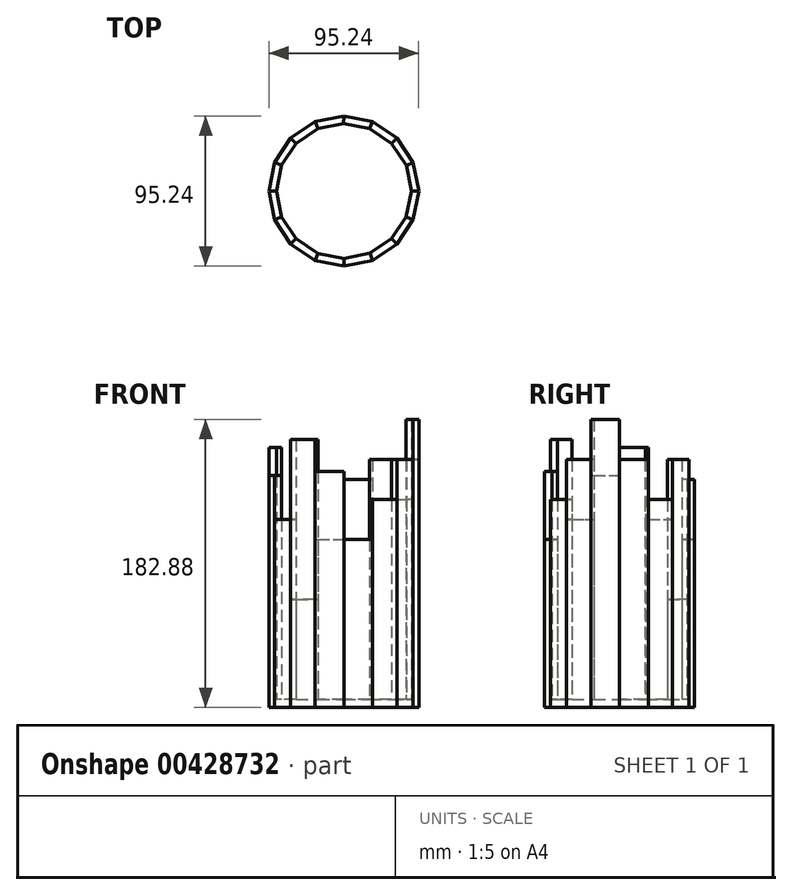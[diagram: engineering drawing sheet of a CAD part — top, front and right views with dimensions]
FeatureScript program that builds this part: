
annotation { "Feature Type Name" : "Feature", "Feature Type Description" : "" }
export const myFeature = defineFeature(function(context is Context, id is Id, definition is map)
    precondition{}
    {
        {
            var Q0;
            Q0=qCreatedBy(makeId("Top.planeOp"),FACE);
            var sketch = newSketch(context, id + "F0", { "sketchPlane" : qUnion([Q0])});
            skLineSegment(sketch, "E0", {"start": v(0, 0) * mm, "end": v(0, 47.63) * mm});
            skLineSegment(sketch, "E1", {"start": v(0, 47.63) * mm, "end": v(0, 0) * mm});
            skLineSegment(sketch, "E2", {"start": v(0, -47.63) * mm, "end": v(0, 0) * mm});
            skLineSegment(sketch, "E3", {"start": v(-47.63, 0) * mm, "end": v(47.63, 0) * mm});
            skLineSegment(sketch, "E4", {"start": v(0, 0) * mm, "end": v(-33.68, 33.68) * mm});
            skLineSegment(sketch, "E5", {"start": v(-33.68, 33.68) * mm, "end": v(0, 0) * mm});
            skLineSegment(sketch, "E6", {"start": v(0, 0) * mm, "end": v(33.68, -33.68) * mm});
            skLineSegment(sketch, "E7", {"start": v(0, 0) * mm, "end": v(33.68, 33.68) * mm});
            skLineSegment(sketch, "E8", {"start": v(0, 0) * mm, "end": v(18.23, 44) * mm});
            skLineSegment(sketch, "E9", {"start": v(0, 0) * mm, "end": v(44, 18.23) * mm});
            skLineSegment(sketch, "E10", {"start": v(0, 0) * mm, "end": v(44, -18.23) * mm});
            skLineSegment(sketch, "E11", {"start": v(0, 0) * mm, "end": v(18.23, -44) * mm});
            skLineSegment(sketch, "E12", {"start": v(0, 0) * mm, "end": v(-33.68, -33.68) * mm});
            skLineSegment(sketch, "E13", {"start": v(0, 0) * mm, "end": v(-18.23, -44) * mm});
            skLineSegment(sketch, "E14", {"start": v(0, 0) * mm, "end": v(-44, -18.23) * mm});
            skLineSegment(sketch, "E15", {"start": v(0, 0) * mm, "end": v(-44, 18.23) * mm});
            skLineSegment(sketch, "E16", {"start": v(0, 0) * mm, "end": v(-18.23, 44) * mm});
            skLineSegment(sketch, "E17", {"start": v(-47.63, 0) * mm, "end": v(-44, 18.23) * mm});
            skLineSegment(sketch, "E18", {"start": v(-44, 18.23) * mm, "end": v(-33.68, 33.68) * mm});
            skLineSegment(sketch, "E19", {"start": v(-18.23, 44) * mm, "end": v(-33.68, 33.68) * mm});
            skLineSegment(sketch, "E20", {"start": v(-18.23, 44) * mm, "end": v(0, 47.63) * mm});
            skLineSegment(sketch, "E21", {"start": v(0, 47.63) * mm, "end": v(18.23, 44) * mm});
            skLineSegment(sketch, "E22", {"start": v(18.23, 44) * mm, "end": v(33.68, 33.68) * mm});
            skLineSegment(sketch, "E23", {"start": v(33.68, 33.68) * mm, "end": v(44, 18.23) * mm});
            skLineSegment(sketch, "E24", {"start": v(44, 18.23) * mm, "end": v(47.63, 0) * mm});
            skLineSegment(sketch, "E25", {"start": v(47.63, 0) * mm, "end": v(44, -18.23) * mm});
            skLineSegment(sketch, "E26", {"start": v(44, -18.23) * mm, "end": v(33.68, -33.68) * mm});
            skLineSegment(sketch, "E27", {"start": v(33.68, -33.68) * mm, "end": v(18.23, -44) * mm});
            skLineSegment(sketch, "E28", {"start": v(18.23, -44) * mm, "end": v(0, -47.63) * mm});
            skLineSegment(sketch, "E29", {"start": v(0, -47.63) * mm, "end": v(-18.23, -44) * mm});
            skLineSegment(sketch, "E30", {"start": v(-18.23, -44) * mm, "end": v(-33.68, -33.68) * mm});
            skLineSegment(sketch, "E31", {"start": v(-33.68, -33.68) * mm, "end": v(-44, -18.23) * mm});
            skLineSegment(sketch, "E32", {"start": v(-44, -18.23) * mm, "end": v(-47.63, 0) * mm});
            skLineSegment(sketch, "E33", {"start": v(-39.6, 16.4) * mm, "end": v(-30.3, 30.3) * mm});
            skLineSegment(sketch, "E34", {"start": v(-30.3, 30.3) * mm, "end": v(-16.4, 39.6) * mm});
            skLineSegment(sketch, "E35", {"start": v(-16.4, 39.6) * mm, "end": v(-0.14, 42.86) * mm});
            skLineSegment(sketch, "E36", {"start": v(-0.14, 42.86) * mm, "end": v(16.4, 39.6) * mm});
            skLineSegment(sketch, "E37", {"start": v(16.4, 39.6) * mm, "end": v(30.3, 30.3) * mm});
            skLineSegment(sketch, "E38", {"start": v(30.3, 30.3) * mm, "end": v(39.69, 16.2) * mm});
            skLineSegment(sketch, "E39", {"start": v(39.69, 16.2) * mm, "end": v(42.86, 0) * mm});
            skLineSegment(sketch, "E40", {"start": v(42.86, 0) * mm, "end": v(39.6, -16.4) * mm});
            skLineSegment(sketch, "E41", {"start": v(39.6, -16.4) * mm, "end": v(30.3, -30.3) * mm});
            skLineSegment(sketch, "E42", {"start": v(30.3, -30.3) * mm, "end": v(16.68, -39.48) * mm});
            skLineSegment(sketch, "E43", {"start": v(16.68, -39.48) * mm, "end": v(0, -42.86) * mm});
            skLineSegment(sketch, "E44", {"start": v(0, -42.86) * mm, "end": v(-16.4, -39.6) * mm});
            skLineSegment(sketch, "E45", {"start": v(-16.4, -39.6) * mm, "end": v(-30.3, -30.3) * mm});
            skLineSegment(sketch, "E46", {"start": v(-30.3, -30.3) * mm, "end": v(-39.6, -16.4) * mm});
            skLineSegment(sketch, "E47", {"start": v(-39.6, -16.4) * mm, "end": v(-42.86, 0) * mm});
            skLineSegment(sketch, "E48", {"start": v(-42.86, 0) * mm, "end": v(-39.6, 16.4) * mm});
            skSolve(sketch);
        }
        {
            var Q0;
            {var subQ1=sQuery(id+"F0.wireOp",EDGE,"E20");Q0=makeQuery(id+"F0.imprint","IMPRINT",FACE,{"disambiguationData":[TD([[makeQuery(id+"F0.imprint","IMPRINT",EDGE,{"derivedFrom":subQ1}),-1.0]])]});}
            var Q1;
            {var subQ0=sQuery(id+"F0.wireOp",EDGE,"E28");Q1=makeQuery(id+"F0.imprint","IMPRINT",FACE,{"disambiguationData":[TD([[makeQuery(id+"F0.imprint","IMPRINT",EDGE,{"derivedFrom":subQ0}),-1.0]])]});}
            var Q2;
            {var subQ0=sQuery(id+"F0.wireOp",EDGE,"E32");Q2=makeQuery(id+"F0.imprint","IMPRINT",FACE,{"disambiguationData":[TD([[makeQuery(id+"F0.imprint","IMPRINT",EDGE,{"derivedFrom":subQ0}),-1.0]])]});}
            var Q3;
            {var subQ4=sQuery(id+"F0.wireOp",EDGE,"E24");Q3=makeQuery(id+"F0.imprint","IMPRINT",FACE,{"disambiguationData":[TD([[makeQuery(id+"F0.imprint","IMPRINT",EDGE,{"derivedFrom":subQ4}),-1.0]])]});}
            var Q4;
            {var subQ0=sQuery(id+"F0.wireOp",EDGE,"E26");Q4=makeQuery(id+"F0.imprint","IMPRINT",FACE,{"disambiguationData":[TD([[makeQuery(id+"F0.imprint","IMPRINT",EDGE,{"derivedFrom":subQ0}),-1.0]])]});}
            var Q5;
            {var subQ0=sQuery(id+"F0.wireOp",EDGE,"E18");Q5=makeQuery(id+"F0.imprint","IMPRINT",FACE,{"disambiguationData":[TD([[makeQuery(id+"F0.imprint","IMPRINT",EDGE,{"derivedFrom":subQ0}),-1.0]])]});}
            var Q6;
            {var subQ0=sQuery(id+"F0.wireOp",EDGE,"E30");Q6=makeQuery(id+"F0.imprint","IMPRINT",FACE,{"disambiguationData":[TD([[makeQuery(id+"F0.imprint","IMPRINT",EDGE,{"derivedFrom":subQ0}),-1.0]])]});}
            var Q7;
            {var subQ0=sQuery(id+"F0.wireOp",EDGE,"E22");Q7=makeQuery(id+"F0.imprint","IMPRINT",FACE,{"disambiguationData":[TD([[makeQuery(id+"F0.imprint","IMPRINT",EDGE,{"derivedFrom":subQ0}),-1.0]])]});}
            var Q8;
            {var subQ0=sQuery(id+"F0.wireOp",EDGE,"E29");Q8=makeQuery(id+"F0.imprint","IMPRINT",FACE,{"disambiguationData":[TD([[makeQuery(id+"F0.imprint","IMPRINT",EDGE,{"derivedFrom":subQ0}),-1.0]])]});}
            var Q9;
            {var subQ0=sQuery(id+"F0.wireOp",EDGE,"E21");Q9=makeQuery(id+"F0.imprint","IMPRINT",FACE,{"disambiguationData":[TD([[makeQuery(id+"F0.imprint","IMPRINT",EDGE,{"derivedFrom":subQ0}),-1.0]])]});}
            var Q10;
            {var subQ0=sQuery(id+"F0.wireOp",EDGE,"E31");Q10=makeQuery(id+"F0.imprint","IMPRINT",FACE,{"disambiguationData":[TD([[makeQuery(id+"F0.imprint","IMPRINT",EDGE,{"derivedFrom":subQ0}),-1.0]])]});}
            var Q11;
            {var subQ0=sQuery(id+"F0.wireOp",EDGE,"E23");Q11=makeQuery(id+"F0.imprint","IMPRINT",FACE,{"disambiguationData":[TD([[makeQuery(id+"F0.imprint","IMPRINT",EDGE,{"derivedFrom":subQ0}),-1.0]])]});}
            var Q12;
            {var subQ1=sQuery(id+"F0.wireOp",EDGE,"E27");Q12=makeQuery(id+"F0.imprint","IMPRINT",FACE,{"disambiguationData":[TD([[makeQuery(id+"F0.imprint","IMPRINT",EDGE,{"derivedFrom":subQ1}),-1.0]])]});}
            var Q13;
            {var subQ0=sQuery(id+"F0.wireOp",EDGE,"E19");Q13=makeQuery(id+"F0.imprint","IMPRINT",FACE,{"disambiguationData":[TD([[makeQuery(id+"F0.imprint","IMPRINT",EDGE,{"derivedFrom":subQ0}),1.0]])]});}
            var Q14;
            {var subQ0=sQuery(id+"F0.wireOp",EDGE,"E17");Q14=makeQuery(id+"F0.imprint","IMPRINT",FACE,{"disambiguationData":[TD([[makeQuery(id+"F0.imprint","IMPRINT",EDGE,{"derivedFrom":subQ0}),-1.0]])]});}
            var Q15;
            {var subQ0=sQuery(id+"F0.wireOp",EDGE,"E25");Q15=makeQuery(id+"F0.imprint","IMPRINT",FACE,{"disambiguationData":[TD([[makeQuery(id+"F0.imprint","IMPRINT",EDGE,{"derivedFrom":subQ0}),-1.0]])]});}
            extrude(context, id + "F1", {"entities" : qUnion([Q0, Q1, Q2, Q3, Q4, Q5, Q6, Q7, Q8, Q9, Q10, Q11, Q12, Q13, Q14, Q15]), "depth" : 152.4 * mm});
        }
        {
            var Q0;
            Q0=makeQuery(id+"F1.opExtrude","CAP_FACE",FACE,{"disambiguationData":[OSD([sQuery(id+"F0.wireOp",EDGE,"E17"),sQuery(id+"F0.wireOp",EDGE,"E18"),sQuery(id+"F0.wireOp",EDGE,"E19"),sQuery(id+"F0.wireOp",EDGE,"E20"),sQuery(id+"F0.wireOp",EDGE,"E21"),sQuery(id+"F0.wireOp",EDGE,"E22"),sQuery(id+"F0.wireOp",EDGE,"E23"),sQuery(id+"F0.wireOp",EDGE,"E24"),sQuery(id+"F0.wireOp",EDGE,"E25"),sQuery(id+"F0.wireOp",EDGE,"E26"),sQuery(id+"F0.wireOp",EDGE,"E27"),sQuery(id+"F0.wireOp",EDGE,"E28"),sQuery(id+"F0.wireOp",EDGE,"E29"),sQuery(id+"F0.wireOp",EDGE,"E30"),sQuery(id+"F0.wireOp",EDGE,"E31"),sQuery(id+"F0.wireOp",EDGE,"E32"),sQuery(id+"F0.wireOp",EDGE,"E33"),sQuery(id+"F0.wireOp",EDGE,"E34"),sQuery(id+"F0.wireOp",EDGE,"E35"),sQuery(id+"F0.wireOp",EDGE,"E36"),sQuery(id+"F0.wireOp",EDGE,"E37"),sQuery(id+"F0.wireOp",EDGE,"E38"),sQuery(id+"F0.wireOp",EDGE,"E39"),sQuery(id+"F0.wireOp",EDGE,"E40"),sQuery(id+"F0.wireOp",EDGE,"E41"),sQuery(id+"F0.wireOp",EDGE,"E42"),sQuery(id+"F0.wireOp",EDGE,"E43"),sQuery(id+"F0.wireOp",EDGE,"E44"),sQuery(id+"F0.wireOp",EDGE,"E45"),sQuery(id+"F0.wireOp",EDGE,"E46"),sQuery(id+"F0.wireOp",EDGE,"E47"),sQuery(id+"F0.wireOp",EDGE,"E48")])],"isStart":false});
            var sketch = newSketch(context, id + "F2", { "sketchPlane" : qUnion([Q0])});
            skLineSegment(sketch, "E49", {"start": v(-18.23, -44) * mm, "end": v(-16.4, -39.6) * mm});
            skLineSegment(sketch, "E50", {"start": v(0, -47.63) * mm, "end": v(0, -42.86) * mm});
            skLineSegment(sketch, "E51", {"start": v(18.23, -44) * mm, "end": v(16.68, -39.48) * mm});
            skLineSegment(sketch, "E52", {"start": v(33.68, -33.68) * mm, "end": v(30.3, -30.3) * mm});
            skLineSegment(sketch, "E53", {"start": v(44, -18.23) * mm, "end": v(39.6, -16.4) * mm});
            skLineSegment(sketch, "E54", {"start": v(47.63, 0) * mm, "end": v(42.86, 0) * mm});
            skLineSegment(sketch, "E55", {"start": v(44, 18.23) * mm, "end": v(39.69, 16.2) * mm});
            skLineSegment(sketch, "E56", {"start": v(33.68, 33.68) * mm, "end": v(30.3, 30.3) * mm});
            skLineSegment(sketch, "E57", {"start": v(18.23, 44) * mm, "end": v(16.4, 39.6) * mm});
            skLineSegment(sketch, "E58", {"start": v(0, 47.63) * mm, "end": v(-0.14, 42.86) * mm});
            skLineSegment(sketch, "E59", {"start": v(-18.23, 44) * mm, "end": v(-16.4, 39.6) * mm});
            skLineSegment(sketch, "E60", {"start": v(-33.68, 33.68) * mm, "end": v(-30.3, 30.3) * mm});
            skLineSegment(sketch, "E61", {"start": v(-39.6, 16.4) * mm, "end": v(-44, 18.23) * mm});
            skLineSegment(sketch, "E62", {"start": v(-47.63, 0) * mm, "end": v(-42.86, 0) * mm});
            skLineSegment(sketch, "E63", {"start": v(-39.6, -16.4) * mm, "end": v(-44, -18.23) * mm});
            skLineSegment(sketch, "E64", {"start": v(-30.3, -30.3) * mm, "end": v(-33.68, -33.68) * mm});
            skSolve(sketch);
        }
        {
            var Q0;
            Q0=makeQuery(id+"F2.imprint","IMPRINT",FACE,{"disambiguationData":[TD([[makeQuery(id+"F2.imprint","IMPRINT",EDGE,{"derivedFrom":sQuery(id+"F2.wireOp",EDGE,"E55")}),-1.0]])]});
            extrude(context, id + "F3", {"entities" : qUnion([Q0]), "operationType" : NewBodyOperationType.REMOVE, "oppositeDirection" : true, "depth" : 25.4 * mm});
        }
        {
            var Q0;
            Q0=makeQuery(id+"F1.opExtrude","CAP_FACE",FACE,{"disambiguationData":[OSD([sQuery(id+"F0.wireOp",EDGE,"E17"),sQuery(id+"F0.wireOp",EDGE,"E18"),sQuery(id+"F0.wireOp",EDGE,"E19"),sQuery(id+"F0.wireOp",EDGE,"E20"),sQuery(id+"F0.wireOp",EDGE,"E21"),sQuery(id+"F0.wireOp",EDGE,"E22"),sQuery(id+"F0.wireOp",EDGE,"E23"),sQuery(id+"F0.wireOp",EDGE,"E24"),sQuery(id+"F0.wireOp",EDGE,"E25"),sQuery(id+"F0.wireOp",EDGE,"E26"),sQuery(id+"F0.wireOp",EDGE,"E27"),sQuery(id+"F0.wireOp",EDGE,"E28"),sQuery(id+"F0.wireOp",EDGE,"E29"),sQuery(id+"F0.wireOp",EDGE,"E30"),sQuery(id+"F0.wireOp",EDGE,"E31"),sQuery(id+"F0.wireOp",EDGE,"E32"),sQuery(id+"F0.wireOp",EDGE,"E33"),sQuery(id+"F0.wireOp",EDGE,"E34"),sQuery(id+"F0.wireOp",EDGE,"E35"),sQuery(id+"F0.wireOp",EDGE,"E36"),sQuery(id+"F0.wireOp",EDGE,"E37"),sQuery(id+"F0.wireOp",EDGE,"E38"),sQuery(id+"F0.wireOp",EDGE,"E39"),sQuery(id+"F0.wireOp",EDGE,"E40"),sQuery(id+"F0.wireOp",EDGE,"E41"),sQuery(id+"F0.wireOp",EDGE,"E42"),sQuery(id+"F0.wireOp",EDGE,"E43"),sQuery(id+"F0.wireOp",EDGE,"E44"),sQuery(id+"F0.wireOp",EDGE,"E45"),sQuery(id+"F0.wireOp",EDGE,"E46"),sQuery(id+"F0.wireOp",EDGE,"E47"),sQuery(id+"F0.wireOp",EDGE,"E48")])],"isStart":false});
            var sketch = newSketch(context, id + "F4", { "sketchPlane" : qUnion([Q0])});
            skLineSegment(sketch, "E65", {"start": v(0, 47.63) * mm, "end": v(-0.14, 42.86) * mm});
            skLineSegment(sketch, "E66", {"start": v(-18.23, 44) * mm, "end": v(-16.4, 39.6) * mm});
            skSolve(sketch);
        }
        {
            var Q0;
            Q0=makeQuery(id+"F4.imprint","IMPRINT",FACE,{"disambiguationData":[TD([[makeQuery(id+"F4.imprint","IMPRINT",EDGE,{"derivedFrom":sQuery(id+"F4.wireOp",EDGE,"E65")}),-1.0]])]});
            extrude(context, id + "F5", {"entities" : qUnion([Q0]), "operationType" : NewBodyOperationType.REMOVE, "oppositeDirection" : true, "depth" : 50.8 * mm});
        }
        {
            var Q0;
            {var subQ0=sQuery(id+"F0.wireOp",EDGE,"E37");var subQ1=sQuery(id+"F0.wireOp",EDGE,"E22");var subQ2=sQuery(id+"F0.wireOp",EDGE,"E36");var subQ3=sQuery(id+"F0.wireOp",EDGE,"E21");Q0=makeQuery(id+"F5.boolean.opBoolean","SPLIT",FACE,{"disambiguationData":[TD([makeQuery(id+"F1.opExtrude","SWEPT_FACE",FACE,{"disambiguationData":[OSD([subQ3])]})])],"derivedFrom":makeQuery(id+"F1.opExtrude","CAP_FACE",FACE,{"disambiguationData":[OSD([sQuery(id+"F0.wireOp",EDGE,"E17"),sQuery(id+"F0.wireOp",EDGE,"E18"),sQuery(id+"F0.wireOp",EDGE,"E19"),sQuery(id+"F0.wireOp",EDGE,"E20"),subQ3,subQ1,sQuery(id+"F0.wireOp",EDGE,"E23"),sQuery(id+"F0.wireOp",EDGE,"E24"),sQuery(id+"F0.wireOp",EDGE,"E25"),sQuery(id+"F0.wireOp",EDGE,"E26"),sQuery(id+"F0.wireOp",EDGE,"E27"),sQuery(id+"F0.wireOp",EDGE,"E28"),sQuery(id+"F0.wireOp",EDGE,"E29"),sQuery(id+"F0.wireOp",EDGE,"E30"),sQuery(id+"F0.wireOp",EDGE,"E31"),sQuery(id+"F0.wireOp",EDGE,"E32"),sQuery(id+"F0.wireOp",EDGE,"E33"),sQuery(id+"F0.wireOp",EDGE,"E34"),sQuery(id+"F0.wireOp",EDGE,"E35"),subQ2,subQ0,sQuery(id+"F0.wireOp",EDGE,"E38"),sQuery(id+"F0.wireOp",EDGE,"E39"),sQuery(id+"F0.wireOp",EDGE,"E40"),sQuery(id+"F0.wireOp",EDGE,"E41"),sQuery(id+"F0.wireOp",EDGE,"E42"),sQuery(id+"F0.wireOp",EDGE,"E43"),sQuery(id+"F0.wireOp",EDGE,"E44"),sQuery(id+"F0.wireOp",EDGE,"E45"),sQuery(id+"F0.wireOp",EDGE,"E46"),sQuery(id+"F0.wireOp",EDGE,"E47"),sQuery(id+"F0.wireOp",EDGE,"E48")])],"isStart":false})});}
            var sketch = newSketch(context, id + "F6", { "sketchPlane" : qUnion([Q0])});
            skLineSegment(sketch, "E67", {"start": v(18.23, 44) * mm, "end": v(16.4, 39.6) * mm});
            skSolve(sketch);
        }
        {
            var Q0;
            Q0=makeQuery(id+"F6.imprint","IMPRINT",FACE,{"disambiguationData":[TD([[makeQuery(id+"F6.imprint","IMPRINT",EDGE,{"derivedFrom":sQuery(id+"F6.wireOp",EDGE,"E67")}),-1.0]])]});
            extrude(context, id + "F7", {"entities" : qUnion([Q0]), "operationType" : NewBodyOperationType.REMOVE, "oppositeDirection" : true, "depth" : 12.7 * mm});
        }
        {
            var Q0;
            {var subQ0=sQuery(id+"F0.wireOp",EDGE,"E46");var subQ1=sQuery(id+"F0.wireOp",EDGE,"E45");var subQ2=sQuery(id+"F0.wireOp",EDGE,"E44");var subQ3=sQuery(id+"F0.wireOp",EDGE,"E43");var subQ4=sQuery(id+"F0.wireOp",EDGE,"E40");var subQ5=sQuery(id+"F0.wireOp",EDGE,"E39");var subQ6=sQuery(id+"F0.wireOp",EDGE,"E34");var subQ7=sQuery(id+"F0.wireOp",EDGE,"E33");var subQ8=sQuery(id+"F0.wireOp",EDGE,"E32");var subQ9=sQuery(id+"F0.wireOp",EDGE,"E31");var subQ10=sQuery(id+"F0.wireOp",EDGE,"E24");var subQ11=sQuery(id+"F0.wireOp",EDGE,"E42");var subQ12=sQuery(id+"F0.wireOp",EDGE,"E19");var subQ13=sQuery(id+"F0.wireOp",EDGE,"E30");var subQ14=sQuery(id+"F0.wireOp",EDGE,"E41");var subQ15=sQuery(id+"F0.wireOp",EDGE,"E18");var subQ16=sQuery(id+"F0.wireOp",EDGE,"E29");var subQ17=sQuery(id+"F0.wireOp",EDGE,"E17");var subQ18=sQuery(id+"F0.wireOp",EDGE,"E26");var subQ19=sQuery(id+"F0.wireOp",EDGE,"E25");var subQ20=sQuery(id+"F0.wireOp",EDGE,"E27");var subQ21=sQuery(id+"F0.wireOp",EDGE,"E28");var subQ22=sQuery(id+"F0.wireOp",EDGE,"E47");var subQ23=sQuery(id+"F0.wireOp",EDGE,"E48");Q0=makeQuery(id+"F5.boolean.opBoolean","SPLIT",FACE,{"disambiguationData":[TD([makeQuery(id+"F1.opExtrude","SWEPT_FACE",FACE,{"disambiguationData":[OSD([subQ17])]})])],"derivedFrom":makeQuery(id+"F1.opExtrude","CAP_FACE",FACE,{"disambiguationData":[OSD([subQ17,subQ15,subQ12,sQuery(id+"F0.wireOp",EDGE,"E20"),sQuery(id+"F0.wireOp",EDGE,"E21"),sQuery(id+"F0.wireOp",EDGE,"E22"),sQuery(id+"F0.wireOp",EDGE,"E23"),subQ10,subQ19,subQ18,subQ20,subQ21,subQ16,subQ13,subQ9,subQ8,subQ7,subQ6,sQuery(id+"F0.wireOp",EDGE,"E35"),sQuery(id+"F0.wireOp",EDGE,"E36"),sQuery(id+"F0.wireOp",EDGE,"E37"),sQuery(id+"F0.wireOp",EDGE,"E38"),subQ5,subQ4,subQ14,subQ11,subQ3,subQ2,subQ1,subQ0,subQ22,subQ23])],"isStart":false})});}
            var sketch = newSketch(context, id + "F8", { "sketchPlane" : qUnion([Q0])});
            skLineSegment(sketch, "E68", {"start": v(-33.68, 33.68) * mm, "end": v(-30.3, 30.3) * mm});
            skSolve(sketch);
        }
        {
            var Q0;
            Q0=makeQuery(id+"F8.imprint","IMPRINT",FACE,{"disambiguationData":[TD([[makeQuery(id+"F8.imprint","IMPRINT",EDGE,{"derivedFrom":sQuery(id+"F8.wireOp",EDGE,"E68")}),1.0]])]});
            extrude(context, id + "F9", {"entities" : qUnion([Q0]), "operationType" : NewBodyOperationType.REMOVE, "oppositeDirection" : true, "depth" : 63.5 * mm});
        }
        {
            var Q0;
            {var subQ0=sQuery(id+"F0.wireOp",EDGE,"E46");var subQ1=sQuery(id+"F0.wireOp",EDGE,"E45");var subQ2=sQuery(id+"F0.wireOp",EDGE,"E44");var subQ3=sQuery(id+"F0.wireOp",EDGE,"E43");var subQ4=sQuery(id+"F0.wireOp",EDGE,"E40");var subQ5=sQuery(id+"F0.wireOp",EDGE,"E39");var subQ6=sQuery(id+"F0.wireOp",EDGE,"E34");var subQ7=sQuery(id+"F0.wireOp",EDGE,"E33");var subQ8=sQuery(id+"F0.wireOp",EDGE,"E32");var subQ9=sQuery(id+"F0.wireOp",EDGE,"E31");var subQ10=sQuery(id+"F0.wireOp",EDGE,"E24");var subQ11=sQuery(id+"F0.wireOp",EDGE,"E42");var subQ12=sQuery(id+"F0.wireOp",EDGE,"E19");var subQ13=sQuery(id+"F0.wireOp",EDGE,"E30");var subQ14=sQuery(id+"F0.wireOp",EDGE,"E41");var subQ15=sQuery(id+"F0.wireOp",EDGE,"E18");var subQ16=sQuery(id+"F0.wireOp",EDGE,"E29");var subQ17=sQuery(id+"F0.wireOp",EDGE,"E17");var subQ18=sQuery(id+"F0.wireOp",EDGE,"E26");var subQ19=sQuery(id+"F0.wireOp",EDGE,"E25");var subQ20=sQuery(id+"F0.wireOp",EDGE,"E27");var subQ21=sQuery(id+"F0.wireOp",EDGE,"E28");var subQ22=sQuery(id+"F0.wireOp",EDGE,"E47");var subQ23=sQuery(id+"F0.wireOp",EDGE,"E48");Q0=makeQuery(id+"F5.boolean.opBoolean","SPLIT",FACE,{"disambiguationData":[TD([makeQuery(id+"F1.opExtrude","SWEPT_FACE",FACE,{"disambiguationData":[OSD([subQ17])]})])],"derivedFrom":makeQuery(id+"F1.opExtrude","CAP_FACE",FACE,{"disambiguationData":[OSD([subQ17,subQ15,subQ12,sQuery(id+"F0.wireOp",EDGE,"E20"),sQuery(id+"F0.wireOp",EDGE,"E21"),sQuery(id+"F0.wireOp",EDGE,"E22"),sQuery(id+"F0.wireOp",EDGE,"E23"),subQ10,subQ19,subQ18,subQ20,subQ21,subQ16,subQ13,subQ9,subQ8,subQ7,subQ6,sQuery(id+"F0.wireOp",EDGE,"E35"),sQuery(id+"F0.wireOp",EDGE,"E36"),sQuery(id+"F0.wireOp",EDGE,"E37"),sQuery(id+"F0.wireOp",EDGE,"E38"),subQ5,subQ4,subQ14,subQ11,subQ3,subQ2,subQ1,subQ0,subQ22,subQ23])],"isStart":false})});}
            var sketch = newSketch(context, id + "F10", { "sketchPlane" : qUnion([Q0])});
            skLineSegment(sketch, "E69", {"start": v(-44, 18.23) * mm, "end": v(-39.6, 16.4) * mm});
            skSolve(sketch);
        }
        {
            var Q0;
            Q0=makeQuery(id+"F10.imprint","IMPRINT",FACE,{"disambiguationData":[TD([[makeQuery(id+"F10.imprint","IMPRINT",EDGE,{"derivedFrom":sQuery(id+"F10.wireOp",EDGE,"E69")}),1.0]])]});
            extrude(context, id + "F11", {"entities" : qUnion([Q0]), "operationType" : NewBodyOperationType.REMOVE, "oppositeDirection" : true, "depth" : 38.1 * mm});
        }
        {
            var Q0;
            {var subQ0=sQuery(id+"F0.wireOp",EDGE,"E46");var subQ1=sQuery(id+"F0.wireOp",EDGE,"E45");var subQ2=sQuery(id+"F0.wireOp",EDGE,"E44");var subQ3=sQuery(id+"F0.wireOp",EDGE,"E43");var subQ4=sQuery(id+"F0.wireOp",EDGE,"E40");var subQ5=sQuery(id+"F0.wireOp",EDGE,"E39");var subQ6=sQuery(id+"F0.wireOp",EDGE,"E34");var subQ7=sQuery(id+"F0.wireOp",EDGE,"E33");var subQ8=sQuery(id+"F0.wireOp",EDGE,"E32");var subQ9=sQuery(id+"F0.wireOp",EDGE,"E31");var subQ10=sQuery(id+"F0.wireOp",EDGE,"E24");var subQ11=sQuery(id+"F0.wireOp",EDGE,"E42");var subQ12=sQuery(id+"F0.wireOp",EDGE,"E19");var subQ13=sQuery(id+"F0.wireOp",EDGE,"E30");var subQ14=sQuery(id+"F0.wireOp",EDGE,"E41");var subQ15=sQuery(id+"F0.wireOp",EDGE,"E18");var subQ16=sQuery(id+"F0.wireOp",EDGE,"E29");var subQ17=sQuery(id+"F0.wireOp",EDGE,"E17");var subQ18=sQuery(id+"F0.wireOp",EDGE,"E26");var subQ19=sQuery(id+"F0.wireOp",EDGE,"E25");var subQ20=sQuery(id+"F0.wireOp",EDGE,"E27");var subQ21=sQuery(id+"F0.wireOp",EDGE,"E28");var subQ22=sQuery(id+"F0.wireOp",EDGE,"E47");var subQ23=sQuery(id+"F0.wireOp",EDGE,"E48");Q0=makeQuery(id+"F5.boolean.opBoolean","SPLIT",FACE,{"disambiguationData":[TD([makeQuery(id+"F1.opExtrude","SWEPT_FACE",FACE,{"disambiguationData":[OSD([subQ17])]})])],"derivedFrom":makeQuery(id+"F1.opExtrude","CAP_FACE",FACE,{"disambiguationData":[OSD([subQ17,subQ15,subQ12,sQuery(id+"F0.wireOp",EDGE,"E20"),sQuery(id+"F0.wireOp",EDGE,"E21"),sQuery(id+"F0.wireOp",EDGE,"E22"),sQuery(id+"F0.wireOp",EDGE,"E23"),subQ10,subQ19,subQ18,subQ20,subQ21,subQ16,subQ13,subQ9,subQ8,subQ7,subQ6,sQuery(id+"F0.wireOp",EDGE,"E35"),sQuery(id+"F0.wireOp",EDGE,"E36"),sQuery(id+"F0.wireOp",EDGE,"E37"),sQuery(id+"F0.wireOp",EDGE,"E38"),subQ5,subQ4,subQ14,subQ11,subQ3,subQ2,subQ1,subQ0,subQ22,subQ23])],"isStart":false})});}
            var sketch = newSketch(context, id + "F12", { "sketchPlane" : qUnion([Q0])});
            skLineSegment(sketch, "E70", {"start": v(-47.63, 0) * mm, "end": v(-42.86, 0) * mm});
            skLineSegment(sketch, "E71", {"start": v(-44, -18.23) * mm, "end": v(-39.6, -16.4) * mm});
            skSolve(sketch);
        }
        {
            var Q0;
            Q0=makeQuery(id+"F12.imprint","IMPRINT",FACE,{"disambiguationData":[TD([[makeQuery(id+"F12.imprint","IMPRINT",EDGE,{"derivedFrom":sQuery(id+"F12.wireOp",EDGE,"E70")}),-1.0]])]});
            extrude(context, id + "F13", {"entities" : qUnion([Q0]), "operationType" : NewBodyOperationType.REMOVE, "oppositeDirection" : true, "depth" : 10.16 * mm});
        }
        {
            var Q0;
            Q0=makeQuery(id+"F1.opExtrude","CAP_FACE",FACE,{"disambiguationData":[OSD([sQuery(id+"F0.wireOp",EDGE,"E17"),sQuery(id+"F0.wireOp",EDGE,"E18"),sQuery(id+"F0.wireOp",EDGE,"E19"),sQuery(id+"F0.wireOp",EDGE,"E20"),sQuery(id+"F0.wireOp",EDGE,"E21"),sQuery(id+"F0.wireOp",EDGE,"E22"),sQuery(id+"F0.wireOp",EDGE,"E23"),sQuery(id+"F0.wireOp",EDGE,"E24"),sQuery(id+"F0.wireOp",EDGE,"E25"),sQuery(id+"F0.wireOp",EDGE,"E26"),sQuery(id+"F0.wireOp",EDGE,"E27"),sQuery(id+"F0.wireOp",EDGE,"E28"),sQuery(id+"F0.wireOp",EDGE,"E29"),sQuery(id+"F0.wireOp",EDGE,"E30"),sQuery(id+"F0.wireOp",EDGE,"E31"),sQuery(id+"F0.wireOp",EDGE,"E32"),sQuery(id+"F0.wireOp",EDGE,"E33"),sQuery(id+"F0.wireOp",EDGE,"E34"),sQuery(id+"F0.wireOp",EDGE,"E35"),sQuery(id+"F0.wireOp",EDGE,"E36"),sQuery(id+"F0.wireOp",EDGE,"E37"),sQuery(id+"F0.wireOp",EDGE,"E38"),sQuery(id+"F0.wireOp",EDGE,"E39"),sQuery(id+"F0.wireOp",EDGE,"E40"),sQuery(id+"F0.wireOp",EDGE,"E41"),sQuery(id+"F0.wireOp",EDGE,"E42"),sQuery(id+"F0.wireOp",EDGE,"E43"),sQuery(id+"F0.wireOp",EDGE,"E44"),sQuery(id+"F0.wireOp",EDGE,"E45"),sQuery(id+"F0.wireOp",EDGE,"E46"),sQuery(id+"F0.wireOp",EDGE,"E47"),sQuery(id+"F0.wireOp",EDGE,"E48")])],"isStart":true});
            var sketch = newSketch(context, id + "F14", { "sketchPlane" : qUnion([Q0])});
            skCircle(sketch, "E72.cCircle", {"center": v(0, 0) * mm, "radius": 47.63 * mm, "construction": true});
            skLineSegment(sketch, "E72.0", {"start": v(0, -47.63) * mm, "end": v(-18.23, -44) * mm});
            skLineSegment(sketch, "E72.1", {"start": v(-18.23, -44) * mm, "end": v(-33.68, -33.68) * mm});
            skLineSegment(sketch, "E72.2", {"start": v(-33.68, -33.68) * mm, "end": v(-44, -18.23) * mm});
            skLineSegment(sketch, "E72.3", {"start": v(-44, -18.23) * mm, "end": v(-47.63, 0) * mm});
            skLineSegment(sketch, "E72.4", {"start": v(-47.63, 0) * mm, "end": v(-44, 18.23) * mm});
            skLineSegment(sketch, "E72.5", {"start": v(-44, 18.23) * mm, "end": v(-33.68, 33.68) * mm});
            skLineSegment(sketch, "E72.6", {"start": v(-33.68, 33.68) * mm, "end": v(-18.23, 44) * mm});
            skLineSegment(sketch, "E72.7", {"start": v(-18.23, 44) * mm, "end": v(0, 47.63) * mm});
            skLineSegment(sketch, "E72.8", {"start": v(0, 47.63) * mm, "end": v(18.23, 44) * mm});
            skLineSegment(sketch, "E72.9", {"start": v(18.23, 44) * mm, "end": v(33.68, 33.68) * mm});
            skLineSegment(sketch, "E72.10", {"start": v(33.68, 33.68) * mm, "end": v(44, 18.23) * mm});
            skLineSegment(sketch, "E72.11", {"start": v(44, 18.23) * mm, "end": v(47.63, 0) * mm});
            skLineSegment(sketch, "E72.12", {"start": v(47.63, 0) * mm, "end": v(44, -18.23) * mm});
            skLineSegment(sketch, "E72.13", {"start": v(44, -18.23) * mm, "end": v(33.68, -33.68) * mm});
            skLineSegment(sketch, "E72.14", {"start": v(33.68, -33.68) * mm, "end": v(18.23, -44) * mm});
            skLineSegment(sketch, "E72.15", {"start": v(18.23, -44) * mm, "end": v(0, -47.63) * mm});
            skSolve(sketch);
        }
        {
            var Q0;
            Q0=makeQuery(id+"F14.imprint","IMPRINT",FACE,{"disambiguationData":[TD([[makeQuery(id+"F14.imprint","IMPRINT",EDGE,{"derivedFrom":makeQuery(id+"F1.opExtrude","CAP_EDGE",EDGE,{"disambiguationData":[OSD([sQuery(id+"F0.wireOp",EDGE,"E33")])],"isStart":true})}),1.0]])]});
            var Q1;
            Q1=makeQuery(id+"F14.imprint","IMPRINT",FACE,{"disambiguationData":[TD([[makeQuery(id+"F14.imprint","IMPRINT",EDGE,{"derivedFrom":sQuery(id+"F14.wireOp",EDGE,"E72.0")}),1.0]])]});
            extrude(context, id + "F15", {"entities" : qUnion([Q0, Q1]), "operationType" : NewBodyOperationType.ADD, "depth" : 5.08 * mm});
        }
        {
            var Q0;
            {var subQ0=sQuery(id+"F0.wireOp",EDGE,"E31");var subQ2=sQuery(id+"F0.wireOp",EDGE,"E30");var subQ4=sQuery(id+"F0.wireOp",EDGE,"E40");var subQ6=sQuery(id+"F0.wireOp",EDGE,"E29");var subQ8=sQuery(id+"F0.wireOp",EDGE,"E39");var subQ10=sQuery(id+"F0.wireOp",EDGE,"E28");var subQ13=sQuery(id+"F0.wireOp",EDGE,"E24");var subQ14=makeQuery(id+"F1.opExtrude","SWEPT_FACE",FACE,{"disambiguationData":[OSD([subQ13])]});var subQ15=sQuery(id+"F0.wireOp",EDGE,"E25");var subQ17=sQuery(id+"F0.wireOp",EDGE,"E26");var subQ19=sQuery(id+"F0.wireOp",EDGE,"E27");var subQ21=sQuery(id+"F0.wireOp",EDGE,"E41");var subQ23=sQuery(id+"F0.wireOp",EDGE,"E42");var subQ25=sQuery(id+"F0.wireOp",EDGE,"E43");var subQ27=sQuery(id+"F0.wireOp",EDGE,"E44");var subQ29=sQuery(id+"F0.wireOp",EDGE,"E45");var subQ31=sQuery(id+"F0.wireOp",EDGE,"E46");var subQ33=sQuery(id+"F0.wireOp",EDGE,"E34");var subQ34=sQuery(id+"F0.wireOp",EDGE,"E33");var subQ35=sQuery(id+"F0.wireOp",EDGE,"E32");var subQ36=sQuery(id+"F0.wireOp",EDGE,"E19");var subQ37=sQuery(id+"F0.wireOp",EDGE,"E18");var subQ38=sQuery(id+"F0.wireOp",EDGE,"E17");var subQ39=sQuery(id+"F0.wireOp",EDGE,"E47");var subQ40=sQuery(id+"F0.wireOp",EDGE,"E48");Q0=makeQuery(id+"F13.boolean.opBoolean","SPLIT",FACE,{"disambiguationData":[TD([subQ14])],"derivedFrom":makeQuery(id+"F5.boolean.opBoolean","SPLIT",FACE,{"disambiguationData":[TD([makeQuery(id+"F1.opExtrude","SWEPT_FACE",FACE,{"disambiguationData":[OSD([subQ38])]})])],"derivedFrom":makeQuery(id+"F1.opExtrude","CAP_FACE",FACE,{"disambiguationData":[OSD([subQ38,subQ37,subQ36,sQuery(id+"F0.wireOp",EDGE,"E20"),sQuery(id+"F0.wireOp",EDGE,"E21"),sQuery(id+"F0.wireOp",EDGE,"E22"),sQuery(id+"F0.wireOp",EDGE,"E23"),subQ13,subQ15,subQ17,subQ19,subQ10,subQ6,subQ2,subQ0,subQ35,subQ34,subQ33,sQuery(id+"F0.wireOp",EDGE,"E35"),sQuery(id+"F0.wireOp",EDGE,"E36"),sQuery(id+"F0.wireOp",EDGE,"E37"),sQuery(id+"F0.wireOp",EDGE,"E38"),subQ8,subQ4,subQ21,subQ23,subQ25,subQ27,subQ29,subQ31,subQ39,subQ40])],"isStart":false})})});}
            var sketch = newSketch(context, id + "F16", { "sketchPlane" : qUnion([Q0])});
            skLineSegment(sketch, "E73", {"start": v(-30.3, -30.3) * mm, "end": v(-33.68, -33.68) * mm});
            skSolve(sketch);
        }
        {
            var Q0;
            Q0=makeQuery(id+"F16.imprint","IMPRINT",FACE,{"disambiguationData":[TD([[makeQuery(id+"F16.imprint","IMPRINT",EDGE,{"derivedFrom":sQuery(id+"F16.wireOp",EDGE,"E73")}),-1.0]])]});
            extrude(context, id + "F17", {"entities" : qUnion([Q0]), "operationType" : NewBodyOperationType.REMOVE, "oppositeDirection" : true, "depth" : 38.1 * mm});
        }
        {
            var Q0;
            Q0=makeQuery(id+"F9.boolean.opBoolean","COPY",FACE,{"derivedFrom":makeQuery(id+"F9.opExtrude","CAP_FACE",FACE,{"disambiguationData":[OSD([sQuery(id+"F0.wireOp",EDGE,"E19"),sQuery(id+"F0.wireOp",EDGE,"E34"),sQuery(id+"F4.wireOp",EDGE,"E66"),sQuery(id+"F8.wireOp",EDGE,"E68")])],"isStart":false})});
            extrude(context, id + "F18", {"entities" : qUnion([Q0]), "operationType" : NewBodyOperationType.REMOVE, "oppositeDirection" : true, "depth" : 25.4 * mm});
        }
        {
            var Q0;
            {var subQ0=sQuery(id+"F0.wireOp",EDGE,"E31");var subQ2=sQuery(id+"F0.wireOp",EDGE,"E30");var subQ4=sQuery(id+"F0.wireOp",EDGE,"E40");var subQ6=sQuery(id+"F0.wireOp",EDGE,"E29");var subQ8=sQuery(id+"F0.wireOp",EDGE,"E39");var subQ10=sQuery(id+"F0.wireOp",EDGE,"E28");var subQ13=sQuery(id+"F0.wireOp",EDGE,"E24");var subQ14=makeQuery(id+"F1.opExtrude","SWEPT_FACE",FACE,{"disambiguationData":[OSD([subQ13])]});var subQ15=sQuery(id+"F0.wireOp",EDGE,"E25");var subQ17=sQuery(id+"F0.wireOp",EDGE,"E26");var subQ19=sQuery(id+"F0.wireOp",EDGE,"E27");var subQ21=sQuery(id+"F0.wireOp",EDGE,"E41");var subQ23=sQuery(id+"F0.wireOp",EDGE,"E42");var subQ25=sQuery(id+"F0.wireOp",EDGE,"E43");var subQ27=sQuery(id+"F0.wireOp",EDGE,"E44");var subQ29=sQuery(id+"F0.wireOp",EDGE,"E45");var subQ31=sQuery(id+"F0.wireOp",EDGE,"E46");var subQ33=sQuery(id+"F0.wireOp",EDGE,"E34");var subQ34=sQuery(id+"F0.wireOp",EDGE,"E33");var subQ35=sQuery(id+"F0.wireOp",EDGE,"E32");var subQ36=sQuery(id+"F0.wireOp",EDGE,"E19");var subQ37=sQuery(id+"F0.wireOp",EDGE,"E18");var subQ38=sQuery(id+"F0.wireOp",EDGE,"E17");var subQ39=sQuery(id+"F0.wireOp",EDGE,"E47");var subQ40=sQuery(id+"F0.wireOp",EDGE,"E48");Q0=makeQuery(id+"F13.boolean.opBoolean","SPLIT",FACE,{"disambiguationData":[TD([subQ14])],"derivedFrom":makeQuery(id+"F5.boolean.opBoolean","SPLIT",FACE,{"disambiguationData":[TD([makeQuery(id+"F1.opExtrude","SWEPT_FACE",FACE,{"disambiguationData":[OSD([subQ38])]})])],"derivedFrom":makeQuery(id+"F1.opExtrude","CAP_FACE",FACE,{"disambiguationData":[OSD([subQ38,subQ37,subQ36,sQuery(id+"F0.wireOp",EDGE,"E20"),sQuery(id+"F0.wireOp",EDGE,"E21"),sQuery(id+"F0.wireOp",EDGE,"E22"),sQuery(id+"F0.wireOp",EDGE,"E23"),subQ13,subQ15,subQ17,subQ19,subQ10,subQ6,subQ2,subQ0,subQ35,subQ34,subQ33,sQuery(id+"F0.wireOp",EDGE,"E35"),sQuery(id+"F0.wireOp",EDGE,"E36"),sQuery(id+"F0.wireOp",EDGE,"E37"),sQuery(id+"F0.wireOp",EDGE,"E38"),subQ8,subQ4,subQ21,subQ23,subQ25,subQ27,subQ29,subQ31,subQ39,subQ40])],"isStart":false})})});}
            var sketch = newSketch(context, id + "F19", { "sketchPlane" : qUnion([Q0])});
            skLineSegment(sketch, "E74", {"start": v(-18.23, -44) * mm, "end": v(-16.4, -39.6) * mm});
            skLineSegment(sketch, "E75", {"start": v(0, -42.86) * mm, "end": v(0, -47.63) * mm});
            skSolve(sketch);
        }
        {
            var Q0;
            Q0=makeQuery(id+"F19.imprint","IMPRINT",FACE,{"disambiguationData":[TD([[makeQuery(id+"F19.imprint","IMPRINT",EDGE,{"derivedFrom":sQuery(id+"F19.wireOp",EDGE,"E74")}),-1.0]])]});
            extrude(context, id + "F20", {"entities" : qUnion([Q0]), "operationType" : NewBodyOperationType.REMOVE, "oppositeDirection" : true, "depth" : 7.62 * mm});
        }
        {
            var Q0;
            {var subQ0=sQuery(id+"F0.wireOp",EDGE,"E43");var subQ2=sQuery(id+"F0.wireOp",EDGE,"E42");var subQ4=sQuery(id+"F0.wireOp",EDGE,"E41");var subQ6=sQuery(id+"F0.wireOp",EDGE,"E40");var subQ8=sQuery(id+"F0.wireOp",EDGE,"E39");var subQ10=sQuery(id+"F0.wireOp",EDGE,"E28");var subQ13=sQuery(id+"F0.wireOp",EDGE,"E24");var subQ14=makeQuery(id+"F1.opExtrude","SWEPT_FACE",FACE,{"disambiguationData":[OSD([subQ13])]});var subQ15=sQuery(id+"F0.wireOp",EDGE,"E25");var subQ17=sQuery(id+"F0.wireOp",EDGE,"E26");var subQ19=sQuery(id+"F0.wireOp",EDGE,"E27");var subQ21=sQuery(id+"F0.wireOp",EDGE,"E31");var subQ23=sQuery(id+"F0.wireOp",EDGE,"E30");var subQ25=sQuery(id+"F0.wireOp",EDGE,"E29");var subQ27=sQuery(id+"F0.wireOp",EDGE,"E44");var subQ29=sQuery(id+"F0.wireOp",EDGE,"E45");var subQ31=sQuery(id+"F0.wireOp",EDGE,"E46");var subQ33=sQuery(id+"F0.wireOp",EDGE,"E34");var subQ34=sQuery(id+"F0.wireOp",EDGE,"E33");var subQ35=sQuery(id+"F0.wireOp",EDGE,"E32");var subQ36=sQuery(id+"F0.wireOp",EDGE,"E19");var subQ37=sQuery(id+"F0.wireOp",EDGE,"E18");var subQ38=sQuery(id+"F0.wireOp",EDGE,"E17");var subQ39=sQuery(id+"F0.wireOp",EDGE,"E47");var subQ40=sQuery(id+"F0.wireOp",EDGE,"E48");Q0=makeQuery(id+"F20.boolean.opBoolean","SPLIT",FACE,{"disambiguationData":[TD([subQ14])],"derivedFrom":makeQuery(id+"F13.boolean.opBoolean","SPLIT",FACE,{"disambiguationData":[TD([subQ14])],"derivedFrom":makeQuery(id+"F5.boolean.opBoolean","SPLIT",FACE,{"disambiguationData":[TD([makeQuery(id+"F1.opExtrude","SWEPT_FACE",FACE,{"disambiguationData":[OSD([subQ38])]})])],"derivedFrom":makeQuery(id+"F1.opExtrude","CAP_FACE",FACE,{"disambiguationData":[OSD([subQ38,subQ37,subQ36,sQuery(id+"F0.wireOp",EDGE,"E20"),sQuery(id+"F0.wireOp",EDGE,"E21"),sQuery(id+"F0.wireOp",EDGE,"E22"),sQuery(id+"F0.wireOp",EDGE,"E23"),subQ13,subQ15,subQ17,subQ19,subQ10,subQ25,subQ23,subQ21,subQ35,subQ34,subQ33,sQuery(id+"F0.wireOp",EDGE,"E35"),sQuery(id+"F0.wireOp",EDGE,"E36"),sQuery(id+"F0.wireOp",EDGE,"E37"),sQuery(id+"F0.wireOp",EDGE,"E38"),subQ8,subQ6,subQ4,subQ2,subQ0,subQ27,subQ29,subQ31,subQ39,subQ40])],"isStart":false})})})});}
            var sketch = newSketch(context, id + "F21", { "sketchPlane" : qUnion([Q0])});
            skLineSegment(sketch, "E76", {"start": v(18.23, -44) * mm, "end": v(16.68, -39.48) * mm});
            skSolve(sketch);
        }
        {
            var Q0;
            Q0=makeQuery(id+"F21.imprint","IMPRINT",FACE,{"disambiguationData":[TD([[makeQuery(id+"F21.imprint","IMPRINT",EDGE,{"derivedFrom":sQuery(id+"F21.wireOp",EDGE,"E76")}),1.0]])]});
            extrude(context, id + "F22", {"entities" : qUnion([Q0]), "operationType" : NewBodyOperationType.REMOVE, "oppositeDirection" : true, "depth" : 50.8 * mm});
        }
        {
            var Q0;
            {var subQ0=sQuery(id+"F0.wireOp",EDGE,"E43");var subQ2=sQuery(id+"F0.wireOp",EDGE,"E42");var subQ4=sQuery(id+"F0.wireOp",EDGE,"E41");var subQ6=sQuery(id+"F0.wireOp",EDGE,"E40");var subQ8=sQuery(id+"F0.wireOp",EDGE,"E39");var subQ10=sQuery(id+"F0.wireOp",EDGE,"E28");var subQ13=sQuery(id+"F0.wireOp",EDGE,"E24");var subQ14=makeQuery(id+"F1.opExtrude","SWEPT_FACE",FACE,{"disambiguationData":[OSD([subQ13])]});var subQ15=sQuery(id+"F0.wireOp",EDGE,"E25");var subQ17=sQuery(id+"F0.wireOp",EDGE,"E26");var subQ19=sQuery(id+"F0.wireOp",EDGE,"E27");var subQ21=sQuery(id+"F0.wireOp",EDGE,"E31");var subQ23=sQuery(id+"F0.wireOp",EDGE,"E30");var subQ25=sQuery(id+"F0.wireOp",EDGE,"E29");var subQ27=sQuery(id+"F0.wireOp",EDGE,"E44");var subQ29=sQuery(id+"F0.wireOp",EDGE,"E45");var subQ31=sQuery(id+"F0.wireOp",EDGE,"E46");var subQ33=sQuery(id+"F0.wireOp",EDGE,"E34");var subQ34=sQuery(id+"F0.wireOp",EDGE,"E33");var subQ35=sQuery(id+"F0.wireOp",EDGE,"E32");var subQ36=sQuery(id+"F0.wireOp",EDGE,"E19");var subQ37=sQuery(id+"F0.wireOp",EDGE,"E18");var subQ38=sQuery(id+"F0.wireOp",EDGE,"E17");var subQ39=sQuery(id+"F0.wireOp",EDGE,"E47");var subQ40=sQuery(id+"F0.wireOp",EDGE,"E48");Q0=makeQuery(id+"F20.boolean.opBoolean","SPLIT",FACE,{"disambiguationData":[TD([subQ14])],"derivedFrom":makeQuery(id+"F13.boolean.opBoolean","SPLIT",FACE,{"disambiguationData":[TD([subQ14])],"derivedFrom":makeQuery(id+"F5.boolean.opBoolean","SPLIT",FACE,{"disambiguationData":[TD([makeQuery(id+"F1.opExtrude","SWEPT_FACE",FACE,{"disambiguationData":[OSD([subQ38])]})])],"derivedFrom":makeQuery(id+"F1.opExtrude","CAP_FACE",FACE,{"disambiguationData":[OSD([subQ38,subQ37,subQ36,sQuery(id+"F0.wireOp",EDGE,"E20"),sQuery(id+"F0.wireOp",EDGE,"E21"),sQuery(id+"F0.wireOp",EDGE,"E22"),sQuery(id+"F0.wireOp",EDGE,"E23"),subQ13,subQ15,subQ17,subQ19,subQ10,subQ25,subQ23,subQ21,subQ35,subQ34,subQ33,sQuery(id+"F0.wireOp",EDGE,"E35"),sQuery(id+"F0.wireOp",EDGE,"E36"),sQuery(id+"F0.wireOp",EDGE,"E37"),sQuery(id+"F0.wireOp",EDGE,"E38"),subQ8,subQ6,subQ4,subQ2,subQ0,subQ27,subQ29,subQ31,subQ39,subQ40])],"isStart":false})})})});}
            var sketch = newSketch(context, id + "F23", { "sketchPlane" : qUnion([Q0])});
            skLineSegment(sketch, "E77", {"start": v(33.68, -33.68) * mm, "end": v(30.3, -30.3) * mm});
            skSolve(sketch);
        }
        {
            var Q0;
            Q0=makeQuery(id+"F23.imprint","IMPRINT",FACE,{"disambiguationData":[TD([[makeQuery(id+"F23.imprint","IMPRINT",EDGE,{"derivedFrom":sQuery(id+"F23.wireOp",EDGE,"E77")}),1.0]])]});
            extrude(context, id + "F24", {"entities" : qUnion([Q0]), "operationType" : NewBodyOperationType.REMOVE, "oppositeDirection" : true, "depth" : 25.4 * mm});
        }
        {
            var Q0;
            {var subQ0=sQuery(id+"F0.wireOp",EDGE,"E43");var subQ2=sQuery(id+"F0.wireOp",EDGE,"E42");var subQ4=sQuery(id+"F0.wireOp",EDGE,"E41");var subQ6=sQuery(id+"F0.wireOp",EDGE,"E40");var subQ8=sQuery(id+"F0.wireOp",EDGE,"E39");var subQ10=sQuery(id+"F0.wireOp",EDGE,"E28");var subQ13=sQuery(id+"F0.wireOp",EDGE,"E24");var subQ14=makeQuery(id+"F1.opExtrude","SWEPT_FACE",FACE,{"disambiguationData":[OSD([subQ13])]});var subQ15=sQuery(id+"F0.wireOp",EDGE,"E25");var subQ17=sQuery(id+"F0.wireOp",EDGE,"E26");var subQ19=sQuery(id+"F0.wireOp",EDGE,"E27");var subQ21=sQuery(id+"F0.wireOp",EDGE,"E31");var subQ23=sQuery(id+"F0.wireOp",EDGE,"E30");var subQ25=sQuery(id+"F0.wireOp",EDGE,"E29");var subQ27=sQuery(id+"F0.wireOp",EDGE,"E44");var subQ29=sQuery(id+"F0.wireOp",EDGE,"E45");var subQ31=sQuery(id+"F0.wireOp",EDGE,"E46");var subQ33=sQuery(id+"F0.wireOp",EDGE,"E34");var subQ34=sQuery(id+"F0.wireOp",EDGE,"E33");var subQ35=sQuery(id+"F0.wireOp",EDGE,"E32");var subQ36=sQuery(id+"F0.wireOp",EDGE,"E19");var subQ37=sQuery(id+"F0.wireOp",EDGE,"E18");var subQ38=sQuery(id+"F0.wireOp",EDGE,"E17");var subQ39=sQuery(id+"F0.wireOp",EDGE,"E47");var subQ40=sQuery(id+"F0.wireOp",EDGE,"E48");Q0=makeQuery(id+"F20.boolean.opBoolean","SPLIT",FACE,{"disambiguationData":[TD([subQ14])],"derivedFrom":makeQuery(id+"F13.boolean.opBoolean","SPLIT",FACE,{"disambiguationData":[TD([subQ14])],"derivedFrom":makeQuery(id+"F5.boolean.opBoolean","SPLIT",FACE,{"disambiguationData":[TD([makeQuery(id+"F1.opExtrude","SWEPT_FACE",FACE,{"disambiguationData":[OSD([subQ38])]})])],"derivedFrom":makeQuery(id+"F1.opExtrude","CAP_FACE",FACE,{"disambiguationData":[OSD([subQ38,subQ37,subQ36,sQuery(id+"F0.wireOp",EDGE,"E20"),sQuery(id+"F0.wireOp",EDGE,"E21"),sQuery(id+"F0.wireOp",EDGE,"E22"),sQuery(id+"F0.wireOp",EDGE,"E23"),subQ13,subQ15,subQ17,subQ19,subQ10,subQ25,subQ23,subQ21,subQ35,subQ34,subQ33,sQuery(id+"F0.wireOp",EDGE,"E35"),sQuery(id+"F0.wireOp",EDGE,"E36"),sQuery(id+"F0.wireOp",EDGE,"E37"),sQuery(id+"F0.wireOp",EDGE,"E38"),subQ8,subQ6,subQ4,subQ2,subQ0,subQ27,subQ29,subQ31,subQ39,subQ40])],"isStart":false})})})});}
            var sketch = newSketch(context, id + "F25", { "sketchPlane" : qUnion([Q0])});
            skLineSegment(sketch, "E78", {"start": v(47.63, 0) * mm, "end": v(42.86, 0) * mm});
            skLineSegment(sketch, "E79", {"start": v(39.6, -16.4) * mm, "end": v(44, -18.23) * mm});
            skSolve(sketch);
        }
        {
            var Q0;
            Q0=makeQuery(id+"F25.imprint","IMPRINT",FACE,{"disambiguationData":[TD([[makeQuery(id+"F25.imprint","IMPRINT",EDGE,{"derivedFrom":sQuery(id+"F25.wireOp",EDGE,"E78")}),1.0]])]});
            extrude(context, id + "F26", {"entities" : qUnion([Q0]), "operationType" : NewBodyOperationType.ADD, "depth" : 25.4 * mm});
        }
        {
            var Q0;
            {var subQ0=sQuery(id+"F0.wireOp",EDGE,"E45");var subQ2=sQuery(id+"F0.wireOp",EDGE,"E30");var subQ3=makeQuery(id+"F1.opExtrude","SWEPT_FACE",FACE,{"disambiguationData":[OSD([subQ2])]});var subQ4=sQuery(id+"F0.wireOp",EDGE,"E31");var subQ6=sQuery(id+"F0.wireOp",EDGE,"E40");var subQ8=sQuery(id+"F0.wireOp",EDGE,"E29");var subQ10=sQuery(id+"F0.wireOp",EDGE,"E39");var subQ12=sQuery(id+"F0.wireOp",EDGE,"E28");var subQ15=sQuery(id+"F0.wireOp",EDGE,"E24");var subQ16=makeQuery(id+"F1.opExtrude","SWEPT_FACE",FACE,{"disambiguationData":[OSD([subQ15])]});var subQ17=sQuery(id+"F0.wireOp",EDGE,"E25");var subQ19=sQuery(id+"F0.wireOp",EDGE,"E26");var subQ21=sQuery(id+"F0.wireOp",EDGE,"E27");var subQ23=sQuery(id+"F0.wireOp",EDGE,"E41");var subQ25=sQuery(id+"F0.wireOp",EDGE,"E42");var subQ27=sQuery(id+"F0.wireOp",EDGE,"E43");var subQ29=sQuery(id+"F0.wireOp",EDGE,"E44");var subQ31=sQuery(id+"F0.wireOp",EDGE,"E46");var subQ33=sQuery(id+"F0.wireOp",EDGE,"E34");var subQ34=sQuery(id+"F0.wireOp",EDGE,"E33");var subQ35=sQuery(id+"F0.wireOp",EDGE,"E32");var subQ36=sQuery(id+"F0.wireOp",EDGE,"E19");var subQ37=sQuery(id+"F0.wireOp",EDGE,"E18");var subQ38=sQuery(id+"F0.wireOp",EDGE,"E17");var subQ39=sQuery(id+"F0.wireOp",EDGE,"E47");var subQ40=sQuery(id+"F0.wireOp",EDGE,"E48");Q0=makeQuery(id+"F20.boolean.opBoolean","SPLIT",FACE,{"disambiguationData":[TD([subQ3])],"derivedFrom":makeQuery(id+"F13.boolean.opBoolean","SPLIT",FACE,{"disambiguationData":[TD([subQ16])],"derivedFrom":makeQuery(id+"F5.boolean.opBoolean","SPLIT",FACE,{"disambiguationData":[TD([makeQuery(id+"F1.opExtrude","SWEPT_FACE",FACE,{"disambiguationData":[OSD([subQ38])]})])],"derivedFrom":makeQuery(id+"F1.opExtrude","CAP_FACE",FACE,{"disambiguationData":[OSD([subQ38,subQ37,subQ36,sQuery(id+"F0.wireOp",EDGE,"E20"),sQuery(id+"F0.wireOp",EDGE,"E21"),sQuery(id+"F0.wireOp",EDGE,"E22"),sQuery(id+"F0.wireOp",EDGE,"E23"),subQ15,subQ17,subQ19,subQ21,subQ12,subQ8,subQ2,subQ4,subQ35,subQ34,subQ33,sQuery(id+"F0.wireOp",EDGE,"E35"),sQuery(id+"F0.wireOp",EDGE,"E36"),sQuery(id+"F0.wireOp",EDGE,"E37"),sQuery(id+"F0.wireOp",EDGE,"E38"),subQ10,subQ6,subQ23,subQ25,subQ27,subQ29,subQ0,subQ31,subQ39,subQ40])],"isStart":false})})})});}
            extrude(context, id + "F27", {"entities" : qUnion([Q0]), "operationType" : NewBodyOperationType.ADD, "depth" : 12.7 * mm});
        }
        {
            var Q0;
            {var subQ0=sQuery(id+"F0.wireOp",EDGE,"E17");var subQ1=makeQuery(id+"F1.opExtrude","SWEPT_FACE",FACE,{"disambiguationData":[OSD([subQ0])]});var subQ2=sQuery(id+"F0.wireOp",EDGE,"E48");var subQ4=sQuery(id+"F0.wireOp",EDGE,"E46");var subQ5=sQuery(id+"F0.wireOp",EDGE,"E45");var subQ6=sQuery(id+"F0.wireOp",EDGE,"E44");var subQ7=sQuery(id+"F0.wireOp",EDGE,"E43");var subQ8=sQuery(id+"F0.wireOp",EDGE,"E40");var subQ9=sQuery(id+"F0.wireOp",EDGE,"E39");var subQ10=sQuery(id+"F0.wireOp",EDGE,"E34");var subQ11=sQuery(id+"F0.wireOp",EDGE,"E33");var subQ12=sQuery(id+"F0.wireOp",EDGE,"E32");var subQ13=sQuery(id+"F0.wireOp",EDGE,"E31");var subQ14=sQuery(id+"F0.wireOp",EDGE,"E24");var subQ15=sQuery(id+"F0.wireOp",EDGE,"E42");var subQ16=sQuery(id+"F0.wireOp",EDGE,"E19");var subQ17=sQuery(id+"F0.wireOp",EDGE,"E30");var subQ18=sQuery(id+"F0.wireOp",EDGE,"E41");var subQ19=sQuery(id+"F0.wireOp",EDGE,"E18");var subQ20=sQuery(id+"F0.wireOp",EDGE,"E29");var subQ21=sQuery(id+"F0.wireOp",EDGE,"E26");var subQ22=sQuery(id+"F0.wireOp",EDGE,"E25");var subQ23=sQuery(id+"F0.wireOp",EDGE,"E27");var subQ24=sQuery(id+"F0.wireOp",EDGE,"E28");var subQ25=sQuery(id+"F0.wireOp",EDGE,"E47");Q0=makeQuery(id+"F13.boolean.opBoolean","SPLIT",FACE,{"disambiguationData":[TD([subQ1])],"derivedFrom":makeQuery(id+"F5.boolean.opBoolean","SPLIT",FACE,{"disambiguationData":[TD([subQ1])],"derivedFrom":makeQuery(id+"F1.opExtrude","CAP_FACE",FACE,{"disambiguationData":[OSD([subQ0,subQ19,subQ16,sQuery(id+"F0.wireOp",EDGE,"E20"),sQuery(id+"F0.wireOp",EDGE,"E21"),sQuery(id+"F0.wireOp",EDGE,"E22"),sQuery(id+"F0.wireOp",EDGE,"E23"),subQ14,subQ22,subQ21,subQ23,subQ24,subQ20,subQ17,subQ13,subQ12,subQ11,subQ10,sQuery(id+"F0.wireOp",EDGE,"E35"),sQuery(id+"F0.wireOp",EDGE,"E36"),sQuery(id+"F0.wireOp",EDGE,"E37"),sQuery(id+"F0.wireOp",EDGE,"E38"),subQ9,subQ8,subQ18,subQ15,subQ7,subQ6,subQ5,subQ4,subQ25,subQ2])],"isStart":false})})});}
            extrude(context, id + "F28", {"entities" : qUnion([Q0]), "operationType" : NewBodyOperationType.ADD, "depth" : 7.62 * mm});
        }
    });
